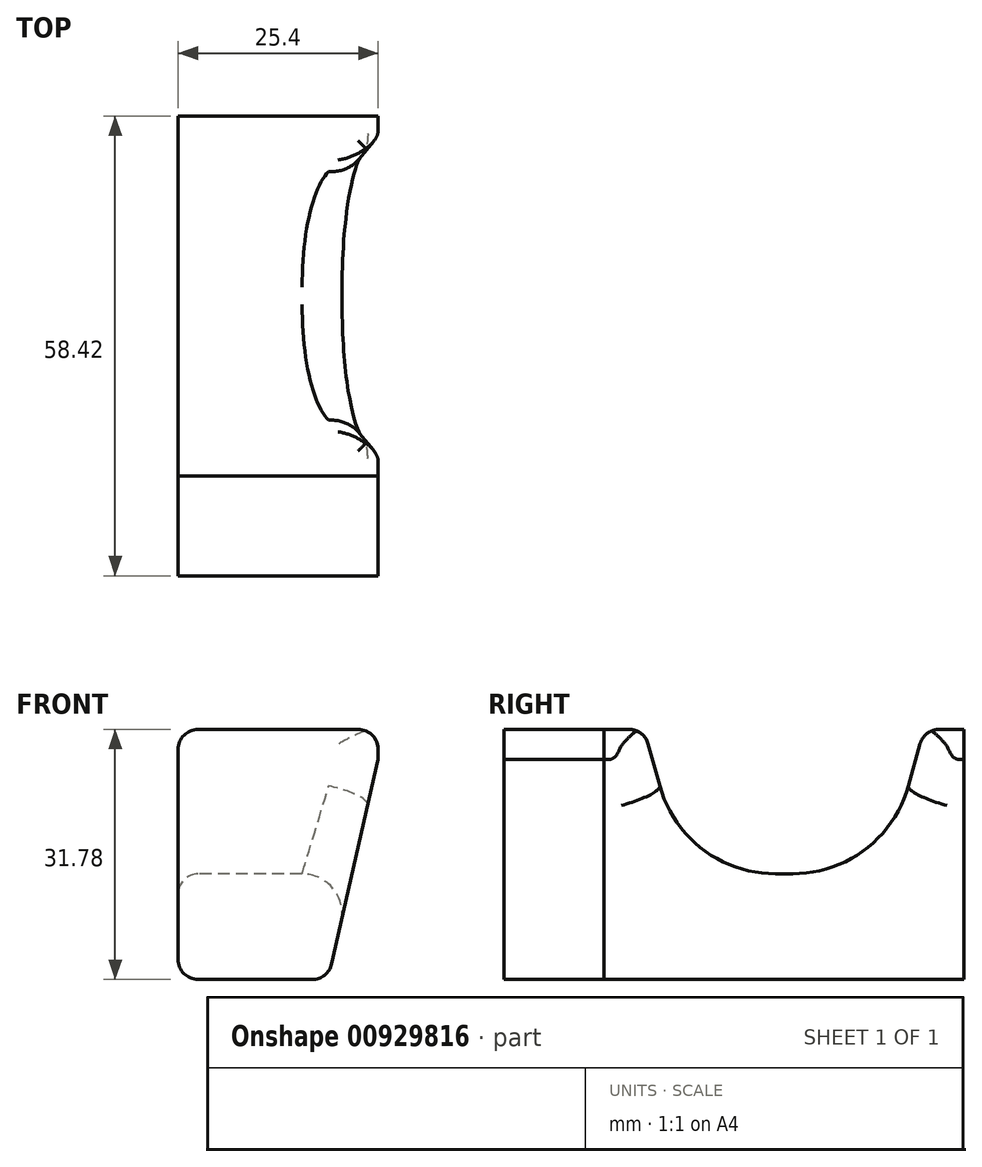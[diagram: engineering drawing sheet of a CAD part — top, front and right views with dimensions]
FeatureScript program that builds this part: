
annotation { "Feature Type Name" : "Feature", "Feature Type Description" : "" }
export const myFeature = defineFeature(function(context is Context, id is Id, definition is map)
    precondition{}
    {
        {
            var Q0;
            Q0=qCreatedBy(makeId("Right.planeOp"),FACE);
            var sketch = newSketch(context, id + "F0", { "sketchPlane" : qUnion([Q0])});
            skLineSegment(sketch, "E0", {"start": v(-11.1, -10.45) * mm, "end": v(14.3, -10.45) * mm});
            skLineSegment(sketch, "E1", {"start": v(14.3, -10.45) * mm, "end": v(19.37, 7.9) * mm});
            skLineSegment(sketch, "E2", {"start": v(19.37, 7.9) * mm, "end": v(24.45, 7.9) * mm});
            skLineSegment(sketch, "E3", {"start": v(24.45, -23.87) * mm, "end": v(-21.27, -23.87) * mm});
            skLineSegment(sketch, "E4", {"start": v(-21.27, -23.87) * mm, "end": v(-21.27, 7.9) * mm});
            skLineSegment(sketch, "E5", {"start": v(-21.27, 7.9) * mm, "end": v(-16.19, 7.9) * mm});
            skLineSegment(sketch, "E6", {"start": v(-16.19, 7.9) * mm, "end": v(-11.1, -10.45) * mm});
            skLineSegment(sketch, "E7", {"start": v(24.45, 7.9) * mm, "end": v(24.45, -23.87) * mm});
            skSolve(sketch);
        }
        {
            var Q0;
            Q0=makeQuery(id+"F0.imprint","IMPRINT",FACE,{"disambiguationData":[TD([[makeQuery(id+"F0.imprint","IMPRINT",EDGE,{"derivedFrom":sQuery(id+"F0.wireOp",EDGE,"E0")}),-1.0]])]});
            extrude(context, id + "F1", {"entities" : qUnion([Q0]), "depth" : 25.4 * mm, "offsetDistance" : 25.4 * mm});
        }
        {
            var Q0;
            Q0=makeQuery(id+"F1.opExtrude","SWEPT_EDGE",EDGE,{"disambiguationData":[OSD([sQuery(id+"F0.wireOp",EDGE,"E0"),sQuery(id+"F0.wireOp",EDGE,"E6")])]});
            var Q1;
            Q1=makeQuery(id+"F1.opExtrude","SWEPT_EDGE",EDGE,{"disambiguationData":[OSD([sQuery(id+"F0.wireOp",EDGE,"E0"),sQuery(id+"F0.wireOp",EDGE,"E1")])]});
            fillet(context, id + "F2", {"entities" : qUnion([Q0, Q1]), "radius" : 15.24 * mm, "tangentPropagation" : true, "allowEdgeOverflow" : false});
        }
        {
            var Q0;
            Q0=makeQuery(id+"F1.opExtrude","CAP_EDGE",EDGE,{"disambiguationData":[OSD([sQuery(id+"F0.wireOp",EDGE,"E3")])],"isStart":false});
            chamfer(context, id + "F3", {"entities" : qUnion([Q0]), "chamferType" : ChamferType.TWO_OFFSETS, "width1" : 6.35 * mm, "oppositeDirection" : false, "width2" : 27.94 * mm, "tangentPropagation" : true});
        }
        {
            var Q0;
            Q0=makeQuery(id+"F1.opExtrude","SWEPT_EDGE",EDGE,{"disambiguationData":[OSD([sQuery(id+"F0.wireOp",EDGE,"E1"),sQuery(id+"F0.wireOp",EDGE,"E2")])]});
            var Q1;
            Q1=makeQuery(id+"F1.opExtrude","SWEPT_EDGE",EDGE,{"disambiguationData":[OSD([sQuery(id+"F0.wireOp",EDGE,"E5"),sQuery(id+"F0.wireOp",EDGE,"E6")])]});
            var Q2;
            Q2=makeQuery(id+"F1.opExtrude","CAP_EDGE",EDGE,{"disambiguationData":[OSD([sQuery(id+"F0.wireOp",EDGE,"E3")])],"isStart":true});
            var Q3;
            {var subQ0=sQuery(id+"F0.wireOp",EDGE,"E3");Q3=makeQuery(id+"F3.opChamfer","BLEND_EDGE",EDGE,{"blendedFrom":[makeQuery(id+"F1.opExtrude","CAP_EDGE",EDGE,{"disambiguationData":[OSD([subQ0])],"isStart":false}),makeQuery(id+"F1.opExtrude","SWEPT_FACE",FACE,{"disambiguationData":[OSD([subQ0])]})],"blendedInto":[makeQuery(id+"F1.opExtrude","SWEPT_FACE",FACE,{"disambiguationData":[OSD([subQ0])]})]});}
            var Q4;
            Q4=makeQuery(id+"F1.opExtrude","CAP_EDGE",EDGE,{"disambiguationData":[OSD([sQuery(id+"F0.wireOp",EDGE,"E5")])],"isStart":true});
            var Q5;
            Q5=makeQuery(id+"F1.opExtrude","CAP_EDGE",EDGE,{"disambiguationData":[OSD([sQuery(id+"F0.wireOp",EDGE,"E5")])],"isStart":false});
            var Q6;
            Q6=makeQuery(id+"F1.opExtrude","CAP_EDGE",EDGE,{"disambiguationData":[OSD([sQuery(id+"F0.wireOp",EDGE,"E2")])],"isStart":true});
            var Q7;
            Q7=makeQuery(id+"F1.opExtrude","CAP_EDGE",EDGE,{"disambiguationData":[OSD([sQuery(id+"F0.wireOp",EDGE,"E2")])],"isStart":false});
            var Q8;
            Q8=makeQuery(id+"F1.opExtrude","CAP_EDGE",EDGE,{"disambiguationData":[OSD([sQuery(id+"F0.wireOp",EDGE,"E1")])],"isStart":true});
            fillet(context, id + "F4", {"entities" : qUnion([Q0, Q1, Q2, Q3, Q4, Q5, Q6, Q7, Q8]), "radius" : 2.54 * mm, "tangentPropagation" : true, "allowEdgeOverflow" : false});
        }
        {
            var Q0;
            Q0=makeQuery(id+"F3.opChamfer","BLEND_EDGE",EDGE,{"blendedFrom":[makeQuery(id+"F1.opExtrude","CAP_EDGE",EDGE,{"disambiguationData":[OSD([sQuery(id+"F0.wireOp",EDGE,"E3")])],"isStart":false}),makeQuery(id+"F1.opExtrude","SWEPT_FACE",FACE,{"disambiguationData":[OSD([sQuery(id+"F0.wireOp",EDGE,"E0")])]})],"blendedInto":[makeQuery(id+"F1.opExtrude","SWEPT_FACE",FACE,{"disambiguationData":[OSD([sQuery(id+"F0.wireOp",EDGE,"E0")])]})]});
            fillet(context, id + "F5", {"entities" : qUnion([Q0]), "radius" : 5.08 * mm, "tangentPropagation" : true, "allowEdgeOverflow" : false});
        }
        {
            var Q0;
            Q0=makeQuery(id+"F1.opExtrude","SWEPT_FACE",FACE,{"disambiguationData":[OSD([sQuery(id+"F0.wireOp",EDGE,"E4")])]});
            extrude(context, id + "F6", {"entities" : qUnion([Q0]), "depth" : 12.7 * mm, "offsetDistance" : 25.4 * mm});
        }
    });
